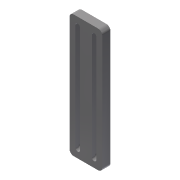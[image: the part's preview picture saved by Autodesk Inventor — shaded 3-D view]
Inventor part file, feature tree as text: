
AUTODESK INVENTOR PART (.ipt)
format: ipt  version: 2015 (Build 190159000, 159)  size: 154,624 bytes
history: native  units: mm
features: extrude x2, sketch x2, fillet x1
ambient origin geometry x8: Origin, YZ Plane, XZ Plane, XY Plane, X Axis, Y Axis, Z Axis, Center Point
bodies: Body1 (feature_tree)
feature tree (5):
  extrude  "Extrusion3"  Depth=150.0mm
  extrude  "Extrusion4"  Depth=10.0mm
  fillet  "Fillet2"  Radius=5.5mm
  sketch  "Sketch5"  dims[d107=40.0mm d108=150.0mm]
  sketch  "Sketch6"  dims[d109=10.0mm d110=10.0mm d111=5.5mm d112=20.0mm d114=130.0mm d115=20.0mm d117=20.0mm d120=10.0mm d121=0.0mm d122=9.0mm d123=9.0mm d124=9.0mm d125=9.0mm d126=6.0mm d127=0.0mm d128=5.0mm]
